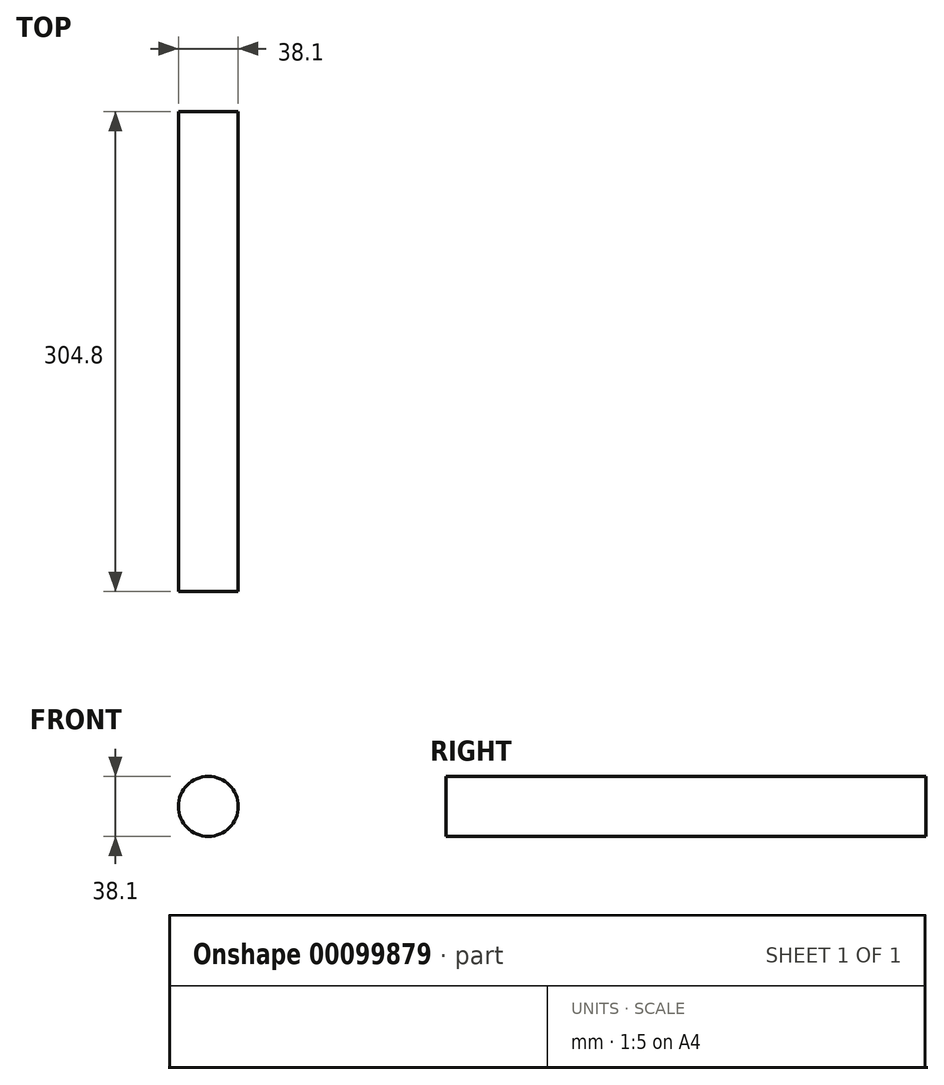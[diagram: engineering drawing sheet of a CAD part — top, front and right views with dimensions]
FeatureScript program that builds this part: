
annotation { "Feature Type Name" : "Feature", "Feature Type Description" : "" }
export const myFeature = defineFeature(function(context is Context, id is Id, definition is map)
    precondition{}
    {
        {
            var Q0;
            Q0=qCreatedBy(makeId("Front.planeOp"),FACE);
            var sketch = newSketch(context, id + "F0", { "sketchPlane" : qUnion([Q0])});
            skCircle(sketch, "E0", {"center": v(0, 0) * mm, "radius": 19.05 * mm});
            skSolve(sketch);
        }
        {
            var Q0;
            Q0 = qSketchRegion(id + "F0", true);
            extrude(context, id + "F1", {"entities" : qUnion([Q0]), "depth" : 304.8 * mm});
        }
    });
